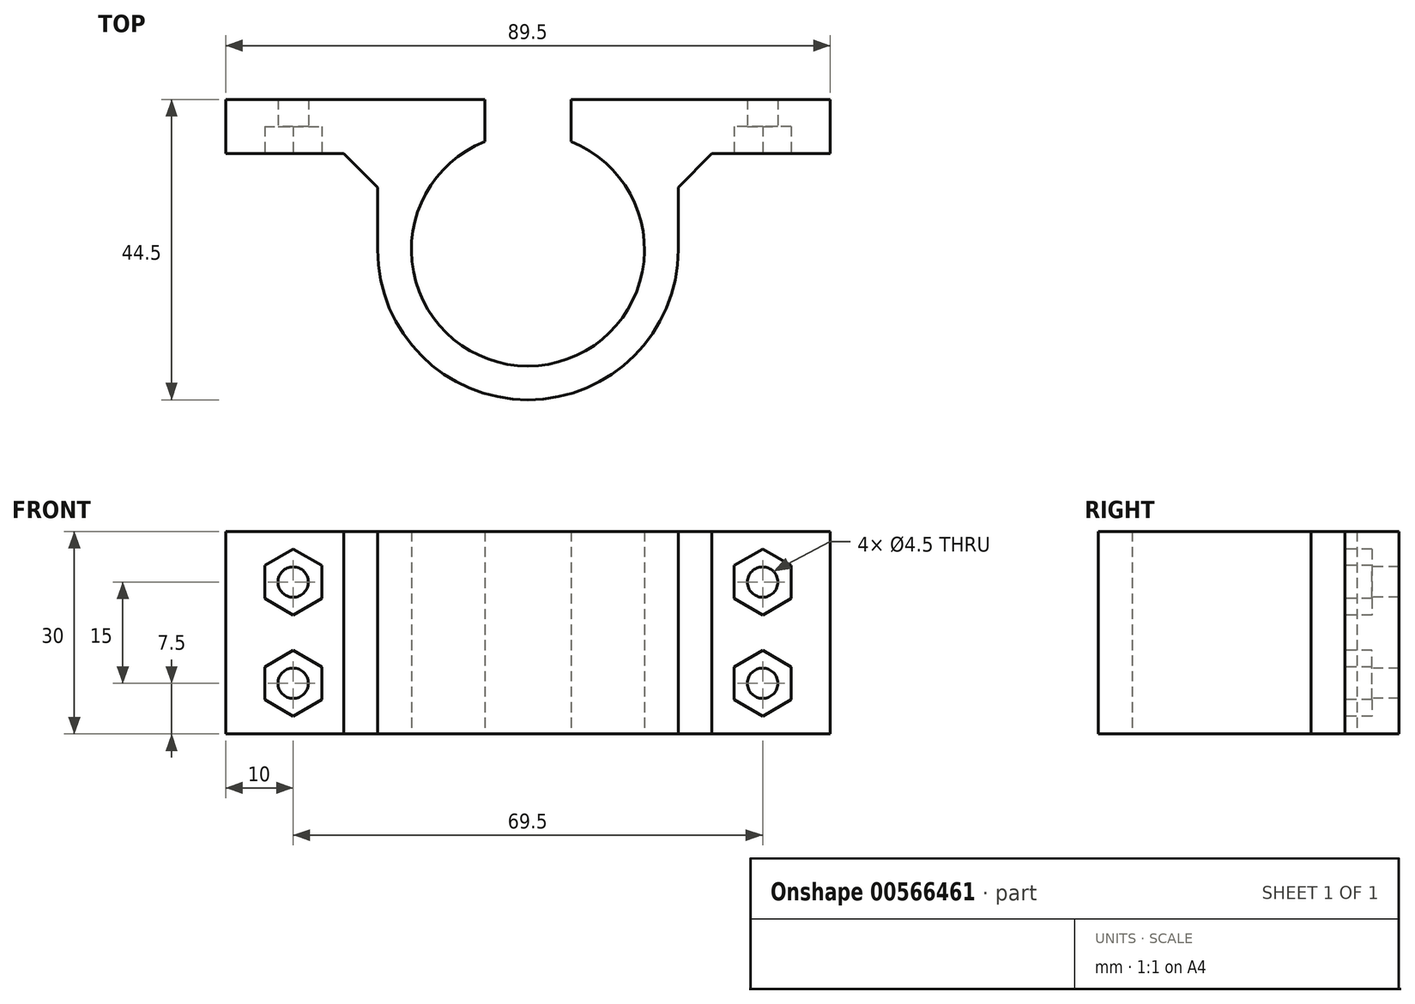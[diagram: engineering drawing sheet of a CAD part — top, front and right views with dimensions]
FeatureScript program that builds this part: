
annotation { "Feature Type Name" : "Feature", "Feature Type Description" : "" }
export const myFeature = defineFeature(function(context is Context, id is Id, definition is map)
    precondition{}
    {
        {
            var Q0;
            Q0=qCreatedBy(makeId("Top.planeOp"),FACE);
            var sketch = newSketch(context, id + "F0", { "sketchPlane" : qUnion([Q0])});
            skArc(sketch, "E0", {"start": v(-6.4, 16.02) * mm, "mid": v(0, -17.25) * mm, "end": v(6.4, 16.02) * mm});
            skArc(sketch, "E1", {"start": v(-22.25, 0) * mm, "mid": v(0, -22.25) * mm, "end": v(22.25, 0) * mm});
            skLineSegment(sketch, "E2", {"start": v(-22.25, 0) * mm, "end": v(-22.25, 14.25) * mm});
            skLineSegment(sketch, "E3", {"start": v(-22.25, 14.25) * mm, "end": v(-44.75, 14.25) * mm, "construction": true});
            skLineSegment(sketch, "E4", {"start": v(-44.75, 14.25) * mm, "end": v(-44.75, 22.25) * mm, "construction": true});
            skLineSegment(sketch, "E5", {"start": v(-44.75, 22.25) * mm, "end": v(-6.4, 22.25) * mm, "construction": true});
            skLineSegment(sketch, "E6.MirrorCS", {"start": v(44.75, 22.25) * mm, "end": v(6.4, 22.25) * mm, "construction": true});
            skLineSegment(sketch, "E7.MirrorCS", {"start": v(44.75, 14.25) * mm, "end": v(44.75, 22.25) * mm, "construction": true});
            skLineSegment(sketch, "E8.MirrorCS", {"start": v(22.25, 14.25) * mm, "end": v(44.75, 14.25) * mm, "construction": true});
            skLineSegment(sketch, "E9.MirrorCS", {"start": v(22.25, 0) * mm, "end": v(22.25, 14.25) * mm});
            skLineSegment(sketch, "E10", {"start": v(-6.4, 16.02) * mm, "end": v(-6.4, 22.25) * mm});
            skLineSegment(sketch, "E11.MirrorCS", {"start": v(6.4, 16.02) * mm, "end": v(6.4, 22.25) * mm});
            skPoint(sketch, "E12.orphan", {"position": v(0, 22.25) * mm});
            skLineSegment(sketch, "E13", {"start": v(-44.75, 14.25) * mm, "end": v(-44.75, 22.25) * mm});
            skLineSegment(sketch, "E14", {"start": v(-44.75, 22.25) * mm, "end": v(-6.4, 22.25) * mm});
            skLineSegment(sketch, "E15", {"start": v(-6.4, 22.25) * mm, "end": v(-6.4, 22.25) * mm});
            skLineSegment(sketch, "E16.MirrorCS", {"start": v(6.4, 22.25) * mm, "end": v(6.4, 22.25) * mm});
            skLineSegment(sketch, "E17.MirrorCS", {"start": v(44.75, 22.25) * mm, "end": v(6.4, 22.25) * mm});
            skLineSegment(sketch, "E18.MirrorCS", {"start": v(44.75, 14.25) * mm, "end": v(44.75, 22.25) * mm});
            skLineSegment(sketch, "E19", {"start": v(-44.75, 14.25) * mm, "end": v(-22.25, 14.25) * mm});
            skLineSegment(sketch, "E20", {"start": v(-22.25, 14.25) * mm, "end": v(-22.25, 14.25) * mm});
            skLineSegment(sketch, "E21.MirrorCS", {"start": v(44.75, 14.25) * mm, "end": v(22.25, 14.25) * mm});
            skLineSegment(sketch, "E22.MirrorCS", {"start": v(22.25, 14.25) * mm, "end": v(22.25, 14.25) * mm});
            skPoint(sketch, "E23.orphan", {"position": v(44.75, 22.25) * mm});
            skSolve(sketch);
        }
        {
            var Q0;
            Q0=qSketchRegion(id+"F0",true);
            extrude(context, id + "F1", {"entities" : qUnion([Q0]), "depth" : 30 * mm, "offsetDistance" : 25 * mm});
        }
        {
            var Q0;
            Q0=makeQuery(id+"F1.opExtrude","SWEPT_FACE",FACE,{"disambiguationData":[OSD([sQuery(id+"F0.wireOp",EDGE,"E19")])]});
            var sketch = newSketch(context, id + "F2", { "sketchPlane" : qUnion([Q0])});
            skCircle(sketch, "E24", {"center": v(-34.75, 22.5) * mm, "radius": 2.25 * mm});
            skCircle(sketch, "E25", {"center": v(-34.75, 7.5) * mm, "radius": 2.25 * mm});
            skCircle(sketch, "E26.MirrorC", {"center": v(34.75, 22.5) * mm, "radius": 2.25 * mm});
            skCircle(sketch, "E27.MirrorC", {"center": v(34.75, 7.5) * mm, "radius": 2.25 * mm});
            skSolve(sketch);
        }
        {
            var Q0;
            Q0=qSketchRegion(id+"F2",true);
            extrude(context, id + "F3", {"entities" : qUnion([Q0]), "operationType" : NewBodyOperationType.REMOVE, "oppositeDirection" : true, "depth" : 25 * mm});
        }
        {
            var Q0;
            Q0=makeQuery(id+"F1.opExtrude","SWEPT_FACE",FACE,{"disambiguationData":[OSD([sQuery(id+"F0.wireOp",EDGE,"E19")])]});
            var sketch = newSketch(context, id + "F4", { "sketchPlane" : qUnion([Q0])});
            skCircle(sketch, "E28.cCircle", {"center": v(-34.75, 22.5) * mm, "radius": 4.22 * mm, "construction": true});
            skLineSegment(sketch, "E28.0", {"start": v(-30.52, 24.94) * mm, "end": v(-30.52, 20.06) * mm});
            skLineSegment(sketch, "E28.1", {"start": v(-30.53, 20.06) * mm, "end": v(-34.75, 17.62) * mm});
            skLineSegment(sketch, "E28.2", {"start": v(-34.75, 17.62) * mm, "end": v(-38.98, 20.06) * mm});
            skLineSegment(sketch, "E28.3", {"start": v(-38.97, 20.06) * mm, "end": v(-38.97, 24.94) * mm});
            skLineSegment(sketch, "E28.4", {"start": v(-38.97, 24.94) * mm, "end": v(-34.75, 27.38) * mm});
            skLineSegment(sketch, "E28.5", {"start": v(-34.75, 27.38) * mm, "end": v(-30.52, 24.94) * mm});
            skPoint(sketch, "E28.0.midPoint", {"position": v(-30.52, 22.5) * mm});
            skCircle(sketch, "E29.cCircle", {"center": v(-34.75, 7.5) * mm, "radius": 4.22 * mm, "construction": true});
            skLineSegment(sketch, "E29.0", {"start": v(-30.52, 9.94) * mm, "end": v(-30.52, 5.06) * mm});
            skLineSegment(sketch, "E29.1", {"start": v(-30.52, 5.06) * mm, "end": v(-34.75, 2.62) * mm});
            skLineSegment(sketch, "E29.2", {"start": v(-34.75, 2.62) * mm, "end": v(-38.97, 5.06) * mm});
            skLineSegment(sketch, "E29.3", {"start": v(-38.97, 5.06) * mm, "end": v(-38.97, 9.94) * mm});
            skLineSegment(sketch, "E29.4", {"start": v(-38.97, 9.94) * mm, "end": v(-34.75, 12.38) * mm});
            skLineSegment(sketch, "E29.5", {"start": v(-34.75, 12.38) * mm, "end": v(-30.52, 9.94) * mm});
            skPoint(sketch, "E29.0.midPoint", {"position": v(-30.52, 7.5) * mm});
            skLineSegment(sketch, "E30.MirrorCS", {"start": v(38.98, 9.94) * mm, "end": v(34.75, 12.38) * mm});
            skLineSegment(sketch, "E31.MirrorCS", {"start": v(38.97, 5.06) * mm, "end": v(38.97, 9.94) * mm});
            skLineSegment(sketch, "E32.MirrorCS", {"start": v(34.75, 2.62) * mm, "end": v(38.97, 5.06) * mm});
            skLineSegment(sketch, "E33.MirrorCS", {"start": v(30.53, 5.06) * mm, "end": v(34.75, 2.62) * mm});
            skLineSegment(sketch, "E34.MirrorCS", {"start": v(30.52, 9.94) * mm, "end": v(30.52, 5.06) * mm});
            skCircle(sketch, "E35.MirrorC", {"center": v(34.75, 7.5) * mm, "radius": 4.22 * mm, "construction": true});
            skCircle(sketch, "E36.MirrorC", {"center": v(34.75, 22.5) * mm, "radius": 4.22 * mm, "construction": true});
            skLineSegment(sketch, "E37.MirrorCS", {"start": v(30.52, 24.94) * mm, "end": v(30.52, 20.06) * mm});
            skLineSegment(sketch, "E38.MirrorCS", {"start": v(30.53, 20.06) * mm, "end": v(34.75, 17.62) * mm});
            skLineSegment(sketch, "E39.MirrorCS", {"start": v(34.75, 17.62) * mm, "end": v(38.97, 20.06) * mm});
            skLineSegment(sketch, "E40.MirrorCS", {"start": v(38.97, 20.06) * mm, "end": v(38.97, 24.94) * mm});
            skLineSegment(sketch, "E41.MirrorCS", {"start": v(38.98, 24.94) * mm, "end": v(34.75, 27.38) * mm});
            skLineSegment(sketch, "E42.MirrorCS", {"start": v(34.75, 27.38) * mm, "end": v(30.52, 24.94) * mm});
            skLineSegment(sketch, "E43.MirrorCS", {"start": v(34.75, 12.38) * mm, "end": v(30.52, 9.94) * mm});
            skPoint(sketch, "E44.MirrorP", {"position": v(30.52, 7.5) * mm});
            skPoint(sketch, "E45.MirrorP", {"position": v(30.52, 22.5) * mm});
            skSolve(sketch);
        }
        {
            var Q0;
            Q0=qSketchRegion(id+"F4",true);
            extrude(context, id + "F5", {"entities" : qUnion([Q0]), "operationType" : NewBodyOperationType.REMOVE, "oppositeDirection" : true, "depth" : 4 * mm});
        }
        {
            var Q0;
            Q0=makeQuery(id+"F1.opExtrude","SWEPT_EDGE",EDGE,{"disambiguationData":[OSD([sQuery(id+"F0.wireOp",EDGE,"E2"),sQuery(id+"F0.wireOp",EDGE,"E19")])]});
            var Q1;
            Q1=makeQuery(id+"F1.opExtrude","SWEPT_EDGE",EDGE,{"disambiguationData":[OSD([sQuery(id+"F0.wireOp",EDGE,"E9.MirrorCS"),sQuery(id+"F0.wireOp",EDGE,"E21.MirrorCS")])]});
            chamfer(context, id + "F6", {"entities" : qUnion([Q0, Q1]), "width" : 5 * mm, "tangentPropagation" : true});
        }
    });
